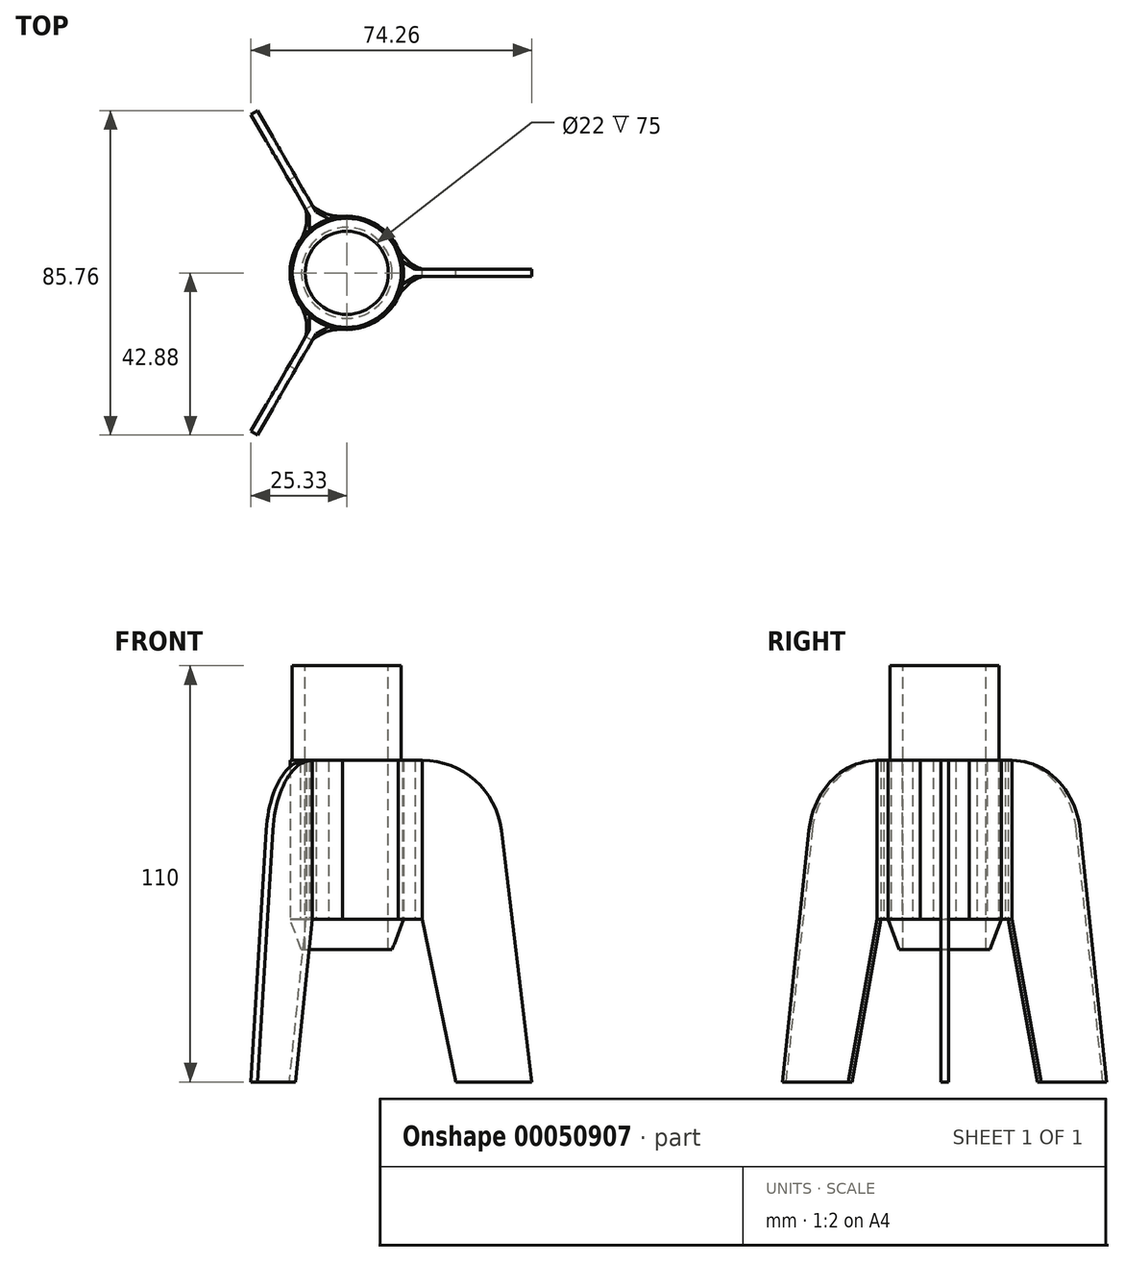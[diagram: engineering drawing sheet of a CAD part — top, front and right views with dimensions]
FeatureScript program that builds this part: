
annotation { "Feature Type Name" : "Feature", "Feature Type Description" : "" }
export const myFeature = defineFeature(function(context is Context, id is Id, definition is map)
    precondition{}
    {
        {
            var Q0;
            Q0=qCreatedBy(makeId("Top.planeOp"),FACE);
            cPlane(context, id + "F0", {"entities" : qUnion([Q0]), "cplaneType" : CPlaneType.OFFSET, "offset" : 35 * mm, "width" : 150 * mm, "height" : 150 * mm});
        }
        {
            var Q0;
            Q0=qCreatedBy(id+"F0.planeOp",FACE);
            var sketch = newSketch(context, id + "F1", { "sketchPlane" : qUnion([Q0])});
            skCircle(sketch, "E0", {"center": v(0, 0) * mm, "radius": 15 * mm});
            skSolve(sketch);
        }
        {
            var Q0;
            Q0 = qSketchRegion(id + "F1", true);
            extrude(context, id + "F2", {"entities" : qUnion([Q0]), "depth" : 50 * mm});
        }
        {
            var Q0;
            Q0=makeQuery(id+"F2.opExtrude","CAP_FACE",FACE,{"disambiguationData":[OSD([sQuery(id+"F1.wireOp",EDGE,"E0")])],"isStart":false});
            var sketch = newSketch(context, id + "F3", { "sketchPlane" : qUnion([Q0])});
            skCircle(sketch, "E1", {"center": v(0, 0) * mm, "radius": 14.4 * mm});
            skSolve(sketch);
        }
        {
            var Q0;
            Q0 = qSketchRegion(id + "F3", true);
            extrude(context, id + "F4", {"entities" : qUnion([Q0]), "operationType" : NewBodyOperationType.ADD, "depth" : 25 * mm});
        }
        {
            var Q0;
            Q0=makeQuery(id+"F4.opExtrude","CAP_FACE",FACE,{"disambiguationData":[OSD([sQuery(id+"F3.wireOp",EDGE,"E1")])],"isStart":false});
            var sketch = newSketch(context, id + "F5", { "sketchPlane" : qUnion([Q0])});
            skCircle(sketch, "E2", {"center": v(0, 0) * mm, "radius": 11 * mm});
            skSolve(sketch);
        }
        {
            var Q0;
            Q0=makeQuery(id+"F5.imprint","IMPRINT",FACE,{"disambiguationData":[TD([[makeQuery(id+"F5.imprint","IMPRINT",EDGE,{"derivedFrom":sQuery(id+"F5.wireOp",EDGE,"E2")}),1.0]])]});
            extrude(context, id + "F6", {"entities" : qUnion([Q0]), "operationType" : NewBodyOperationType.REMOVE, "endBound" : BoundingType.THROUGH_ALL, "oppositeDirection" : true, "depth" : 25 * mm});
        }
        {
            var Q0;
            Q0=makeQuery(id+"F2.opExtrude","CAP_EDGE",EDGE,{"disambiguationData":[OSD([sQuery(id+"F1.wireOp",EDGE,"E0")])],"isStart":true});
            chamfer(context, id + "F7", {"entities" : qUnion([Q0]), "chamferType" : ChamferType.TWO_OFFSETS, "width1" : 3 * mm, "oppositeDirection" : true, "width2" : 8 * mm, "tangentPropagation" : true});
        }
        {
            var Q0;
            Q0=qCreatedBy(makeId("Front.planeOp"),FACE);
            var sketch = newSketch(context, id + "F8", { "sketchPlane" : qUnion([Q0])});
            skLineSegment(sketch, "E3", {"start": v(15, 85) * mm, "end": v(15, 43) * mm});
            skLineSegment(sketch, "E4", {"start": v(-15, 43) * mm, "end": v(-15, 85) * mm});
            skLineSegment(sketch, "E5", {"start": v(15, 43) * mm, "end": v(20, 43) * mm});
            skLineSegment(sketch, "E6", {"start": v(20, 43) * mm, "end": v(28.88, 0) * mm});
            skLineSegment(sketch, "E7", {"start": v(48.93, 0) * mm, "end": v(40.85, 66.53) * mm});
            skPoint(sketch, "E8", {"position": v(15, 64) * mm});
            skLineSegment(sketch, "E9", {"start": v(15, 85) * mm, "end": v(20, 85) * mm});
            skArc(sketch, "E10", {"start": v(20, 85) * mm, "mid": v(33.92, 79.72) * mm, "end": v(40.85, 66.53) * mm});
            skLineSegment(sketch, "E11", {"start": v(0, 56.27) * mm, "end": v(0, -20.68) * mm});
            skLineSegment(sketch, "E12", {"start": v(-35.13, 0) * mm, "end": v(56.25, 0) * mm});
            skSolve(sketch);
        }
        {
            var Q0;
            Q0=makeQuery(id+"F8.imprint","IMPRINT",FACE,{"disambiguationData":[TD([[makeQuery(id+"F8.imprint","IMPRINT",EDGE,{"derivedFrom":sQuery(id+"F8.wireOp",EDGE,"E3")}),1.0]])]});
            extrude(context, id + "F9", {"entities" : qUnion([Q0]), "endBound" : BoundingType.SYMMETRIC, "depth" : 2 * mm});
        }
        {
            var Q0;
            Q0=makeQuery(id+"F9.opExtrude","SWEPT_FACE",FACE,{"disambiguationData":[OSD([sQuery(id+"F8.wireOp",EDGE,"E5")])]});
            var sketch = newSketch(context, id + "F10", { "sketchPlane" : qUnion([Q0])});
            skLineSegment(sketch, "E13.0.0", {"start": v(15, -1) * mm, "end": v(18, -1) * mm});
            skLineSegment(sketch, "E13.0.2", {"start": v(18, 1) * mm, "end": v(15, 1) * mm});
            skArc(sketch, "E14.0", {"start": v(14.7, -3) * mm, "mid": v(15, 0) * mm, "end": v(14.7, 3) * mm});
            skLineSegment(sketch, "E15", {"start": v(18, 1) * mm, "end": v(14.7, 3) * mm});
            skLineSegment(sketch, "E16", {"start": v(18, -1) * mm, "end": v(14.7, -3) * mm});
            skSolve(sketch);
        }
        {
            var Q0;
            {var subQ0=sQuery(id+"F10.wireOp",EDGE,"E13.0.2");Q0=makeQuery(id+"F10.imprint","IMPRINT",FACE,{"disambiguationData":[TD([[makeQuery(id+"F10.imprint","IMPRINT",EDGE,{"derivedFrom":subQ0}),1.0]])]});}
            var Q1;
            {var subQ0=sQuery(id+"F10.wireOp",EDGE,"E13.0.0");Q1=makeQuery(id+"F10.imprint","IMPRINT",FACE,{"disambiguationData":[TD([[makeQuery(id+"F10.imprint","IMPRINT",EDGE,{"derivedFrom":subQ0}),-1.0]])]});}
            var Q2;
            Q2=makeQuery(id+"F9.opExtrude","SWEPT_FACE",FACE,{"disambiguationData":[OSD([sQuery(id+"F8.wireOp",EDGE,"E9")])]});
            extrude(context, id + "F11", {"entities" : qUnion([Q0, Q1]), "endBound" : BoundingType.UP_TO_SURFACE, "oppositeDirection" : true, "endBoundEntityFace" : qUnion([Q2]), "depth" : 25 * mm});
        }
        {
            var Q0;
            Q0=makeQuery(id+"F9.opExtrude","SWEPT_BODY",BODY,{"disambiguationData":[OSD([sQuery(id+"F8.wireOp",EDGE,"E3"),sQuery(id+"F8.wireOp",EDGE,"E5"),sQuery(id+"F8.wireOp",EDGE,"E6"),sQuery(id+"F8.wireOp",EDGE,"4b3e47ce-d8db-44d7-b237-b2970199d4d5"),sQuery(id+"F8.wireOp",EDGE,"E7"),sQuery(id+"F8.wireOp",EDGE,"E9"),sQuery(id+"F8.wireOp",EDGE,"E10")])]});
            var Q1;
            Q1=makeQuery(id+"F11.opExtrude","SWEPT_BODY",BODY,{"disambiguationData":[OSD([sQuery(id+"F8.wireOp",EDGE,"E3"),sQuery(id+"F8.wireOp",EDGE,"E5"),sQuery(id+"F10.wireOp",EDGE,"E13.0.2"),sQuery(id+"F10.wireOp",EDGE,"E14.0"),sQuery(id+"F10.wireOp",EDGE,"E15")])]});
            var Q2;
            Q2=makeQuery(id+"F11.opExtrude","SWEPT_BODY",BODY,{"disambiguationData":[OSD([sQuery(id+"F8.wireOp",EDGE,"E3"),sQuery(id+"F8.wireOp",EDGE,"E5"),sQuery(id+"F10.wireOp",EDGE,"E13.0.0"),sQuery(id+"F10.wireOp",EDGE,"E14.0"),sQuery(id+"F10.wireOp",EDGE,"E16")])]});
            booleanBodies(context, id + "F12", {"operationType" : BooleanOperationType.UNION, "tools" : qUnion([Q0, Q1, Q2])});
        }
        {
            var Q0;
            Q0=makeQuery(id+"F9.opExtrude","SWEPT_BODY",BODY,{"disambiguationData":[OSD([sQuery(id+"F8.wireOp",EDGE,"E3"),sQuery(id+"F8.wireOp",EDGE,"E5"),sQuery(id+"F8.wireOp",EDGE,"E6"),sQuery(id+"F8.wireOp",EDGE,"4b3e47ce-d8db-44d7-b237-b2970199d4d5"),sQuery(id+"F8.wireOp",EDGE,"E7"),sQuery(id+"F8.wireOp",EDGE,"E9"),sQuery(id+"F8.wireOp",EDGE,"E10")])]});
            var Q1;
            Q1=sQuery(id+"F8.wireOp",EDGE,"E11");
            circularPattern(context, id + "F13", {"entities" : qUnion([Q0]), "axis" : qUnion([Q1]), "angle" : 360 * degree, "instanceCount" : 3, "equalSpace" : true});
        }
        {
            var Q0;
            {var subQ0=sQuery(id+"F10.wireOp",EDGE,"E14.0");var subQ1=sQuery(id+"F8.wireOp",EDGE,"E5");var subQ2=sQuery(id+"F8.wireOp",EDGE,"E3");Q0=makeQuery(id+"F12.opBoolean","MERGE",FACE,{"derivedFrom":[makeQuery(id+"F9.opExtrude","SWEPT_FACE",FACE,{"disambiguationData":[OSD([subQ1])]}),makeQuery(id+"F11.opExtrude","CAP_FACE",FACE,{"disambiguationData":[OSD([subQ2,subQ1,sQuery(id+"F10.wireOp",EDGE,"E13.0.0"),subQ0,sQuery(id+"F10.wireOp",EDGE,"E16")])],"isStart":true}),makeQuery(id+"F11.opExtrude","CAP_FACE",FACE,{"disambiguationData":[OSD([subQ2,subQ1,sQuery(id+"F10.wireOp",EDGE,"E13.0.2"),subQ0,sQuery(id+"F10.wireOp",EDGE,"E15")])],"isStart":true})]});}
            var sketch = newSketch(context, id + "F14", { "sketchPlane" : qUnion([Q0])});
            skCircle(sketch, "E17.0", {"center": v(0, 0) * mm, "radius": 15 * mm});
            skLineSegment(sketch, "E18.0", {"start": v(18, 1) * mm, "end": v(14.7, 3) * mm});
            skLineSegment(sketch, "E19.0", {"start": v(18, 1) * mm, "end": v(20, 1) * mm});
            skArc(sketch, "E20", {"start": v(13.54, 6.45) * mm, "mid": v(16.24, 3.1) * mm, "end": v(20, 1) * mm});
            skSolve(sketch);
        }
        {
            var Q0;
            {var subQ0=sQuery(id+"F14.wireOp",EDGE,"E18.0");Q0=makeQuery(id+"F14.imprint","IMPRINT",FACE,{"disambiguationData":[TD([[makeQuery(id+"F14.imprint","IMPRINT",EDGE,{"derivedFrom":subQ0}),-1.0]])]});}
            var Q1;
            {var subQ0=sQuery(id+"F10.wireOp",EDGE,"E14.0");var subQ1=sQuery(id+"F8.wireOp",EDGE,"E5");var subQ2=sQuery(id+"F8.wireOp",EDGE,"E3");Q1=makeQuery(id+"F12.opBoolean","MERGE",FACE,{"derivedFrom":[makeQuery(id+"F9.opExtrude","SWEPT_FACE",FACE,{"disambiguationData":[OSD([sQuery(id+"F8.wireOp",EDGE,"E9")])]}),makeQuery(id+"F11.opExtrude","CAP_FACE",FACE,{"disambiguationData":[OSD([subQ2,subQ1,sQuery(id+"F10.wireOp",EDGE,"E13.0.0"),subQ0,sQuery(id+"F10.wireOp",EDGE,"E16")])],"isStart":false}),makeQuery(id+"F11.opExtrude","CAP_FACE",FACE,{"disambiguationData":[OSD([subQ2,subQ1,sQuery(id+"F10.wireOp",EDGE,"E13.0.2"),subQ0,sQuery(id+"F10.wireOp",EDGE,"E15")])],"isStart":false})]});}
            extrude(context, id + "F15", {"entities" : qUnion([Q0]), "endBound" : BoundingType.UP_TO_SURFACE, "oppositeDirection" : true, "endBoundEntityFace" : qUnion([Q1]), "depth" : 25 * mm});
        }
        {
            var Q0;
            Q0=makeQuery(id+"F15.opExtrude","SWEPT_BODY",BODY,{"disambiguationData":[OSD([sQuery(id+"F14.wireOp",EDGE,"E17.0"),sQuery(id+"F14.wireOp",EDGE,"E18.0"),sQuery(id+"F14.wireOp",EDGE,"E19.0"),sQuery(id+"F14.wireOp",EDGE,"E20")])]});
            var Q1;
            Q1=qCreatedBy(makeId("Front.planeOp"),FACE);
            mirror(context, id + "F16", {"entities" : qUnion([Q0]), "mirrorPlane" : qUnion([Q1])});
        }
        {
            var Q0;
            Q0=makeQuery(id+"F15.opExtrude","SWEPT_BODY",BODY,{"disambiguationData":[OSD([sQuery(id+"F14.wireOp",EDGE,"E17.0"),sQuery(id+"F14.wireOp",EDGE,"E18.0"),sQuery(id+"F14.wireOp",EDGE,"E19.0"),sQuery(id+"F14.wireOp",EDGE,"E20")])]});
            var Q1;
            Q1=makeQuery(id+"F16.opPattern","COPY",BODY,{"derivedFrom":makeQuery(id+"F15.opExtrude","SWEPT_BODY",BODY,{"disambiguationData":[OSD([sQuery(id+"F14.wireOp",EDGE,"E17.0"),sQuery(id+"F14.wireOp",EDGE,"E18.0"),sQuery(id+"F14.wireOp",EDGE,"E19.0"),sQuery(id+"F14.wireOp",EDGE,"E20")])]}),"instanceName":"1"});
            var Q2;
            Q2=sQuery(id+"F8.wireOp",EDGE,"E11");
            circularPattern(context, id + "F17", {"entities" : qUnion([Q0, Q1]), "axis" : qUnion([Q2]), "angle" : 360 * degree, "instanceCount" : 3, "equalSpace" : true});
        }
    });
